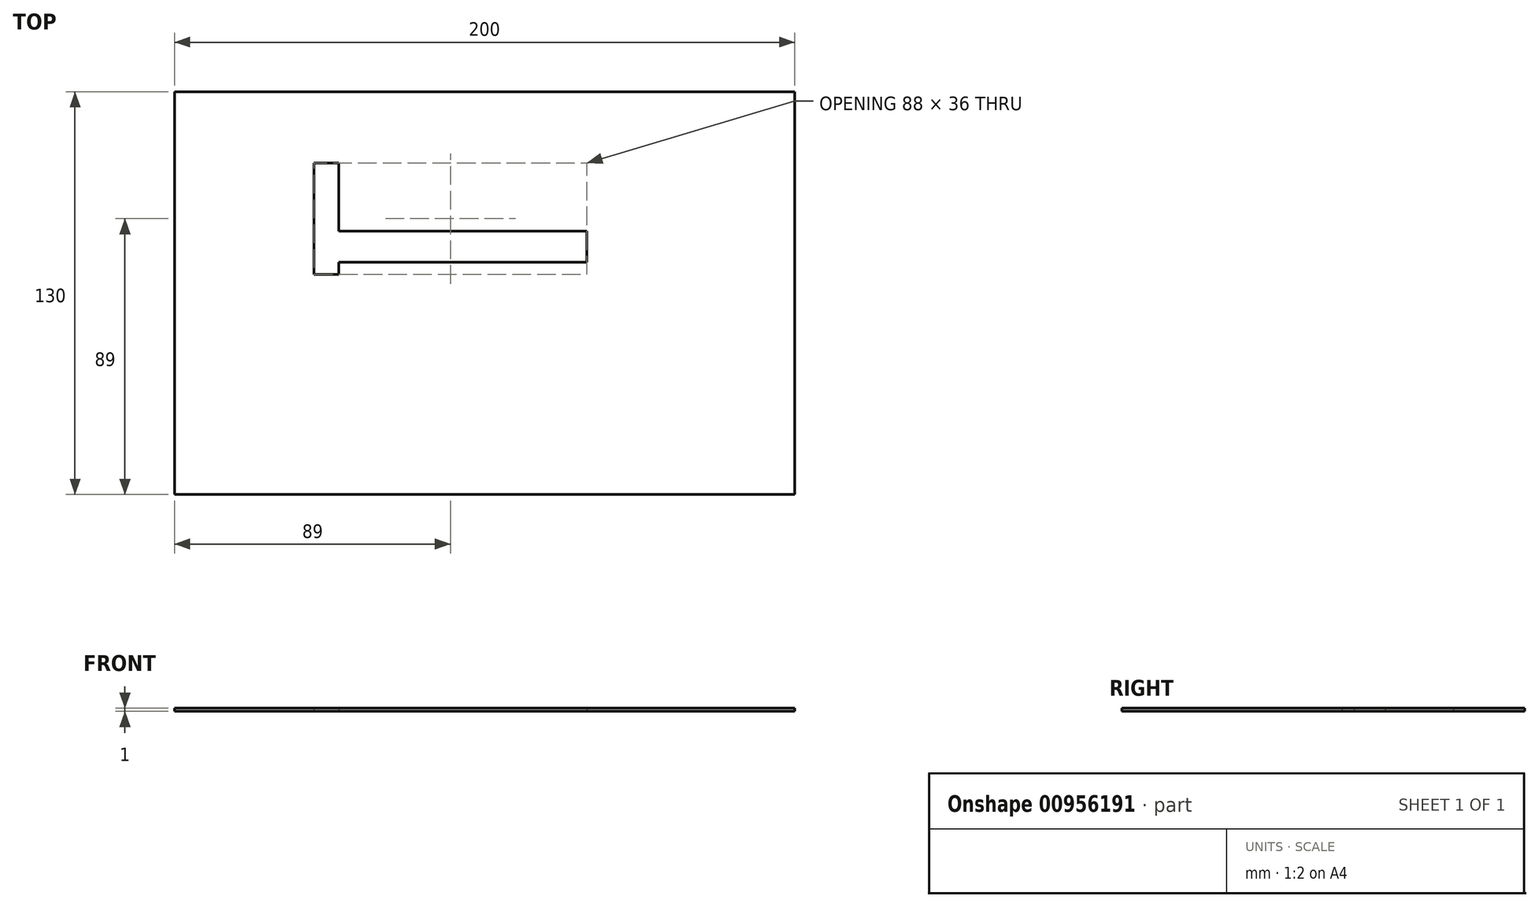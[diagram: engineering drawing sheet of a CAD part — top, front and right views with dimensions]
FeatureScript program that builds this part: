
annotation { "Feature Type Name" : "Feature", "Feature Type Description" : "" }
export const myFeature = defineFeature(function(context is Context, id is Id, definition is map)
    precondition{}
    {
        {
            var Q0;
            Q0=qCreatedBy(makeId("Top.planeOp"),FACE);
            var sketch = newSketch(context, id + "F0", { "sketchPlane" : qUnion([Q0])});
            skLineSegment(sketch, "E0.bottom", {"start": v(100, -65) * mm, "end": v(-100, -65) * mm});
            skLineSegment(sketch, "E0.top", {"start": v(100, 65) * mm, "end": v(-100, 65) * mm});
            skLineSegment(sketch, "E0.left", {"start": v(100, -65) * mm, "end": v(100, 65) * mm});
            skLineSegment(sketch, "E0.right", {"start": v(-100, -65) * mm, "end": v(-100, 65) * mm});
            skPoint(sketch, "E0.middle", {"position": v(0, 0) * mm});
            skLineSegment(sketch, "E1.bottom", {"start": v(-47, 42) * mm, "end": v(-55, 42) * mm});
            skLineSegment(sketch, "E1.top", {"start": v(-47, 6) * mm, "end": v(-55, 6) * mm});
            skLineSegment(sketch, "E1.left", {"start": v(-47, 42) * mm, "end": v(-47, 6) * mm});
            skLineSegment(sketch, "E1.right", {"start": v(-55, 42) * mm, "end": v(-55, 6) * mm});
            skLineSegment(sketch, "E2.bottom", {"start": v(-47, 20) * mm, "end": v(33, 20) * mm});
            skLineSegment(sketch, "E2.top", {"start": v(-47, 10) * mm, "end": v(33, 10) * mm});
            skLineSegment(sketch, "E2.left", {"start": v(-47, 20) * mm, "end": v(-47, 10) * mm});
            skLineSegment(sketch, "E2.right", {"start": v(33, 20) * mm, "end": v(33, 10) * mm});
            skSolve(sketch);
        }
        {
            var Q0;
            Q0=makeQuery(id+"F0.imprint","IMPRINT",FACE,{"disambiguationData":[TD([[makeQuery(id+"F0.imprint","IMPRINT",EDGE,{"derivedFrom":sQuery(id+"F0.wireOp",EDGE,"E0.bottom")}),-1.0]])]});
            extrude(context, id + "F1", {"entities" : qUnion([Q0]), "depth" : 1 * mm, "offsetDistance" : 25 * mm});
        }
    });
